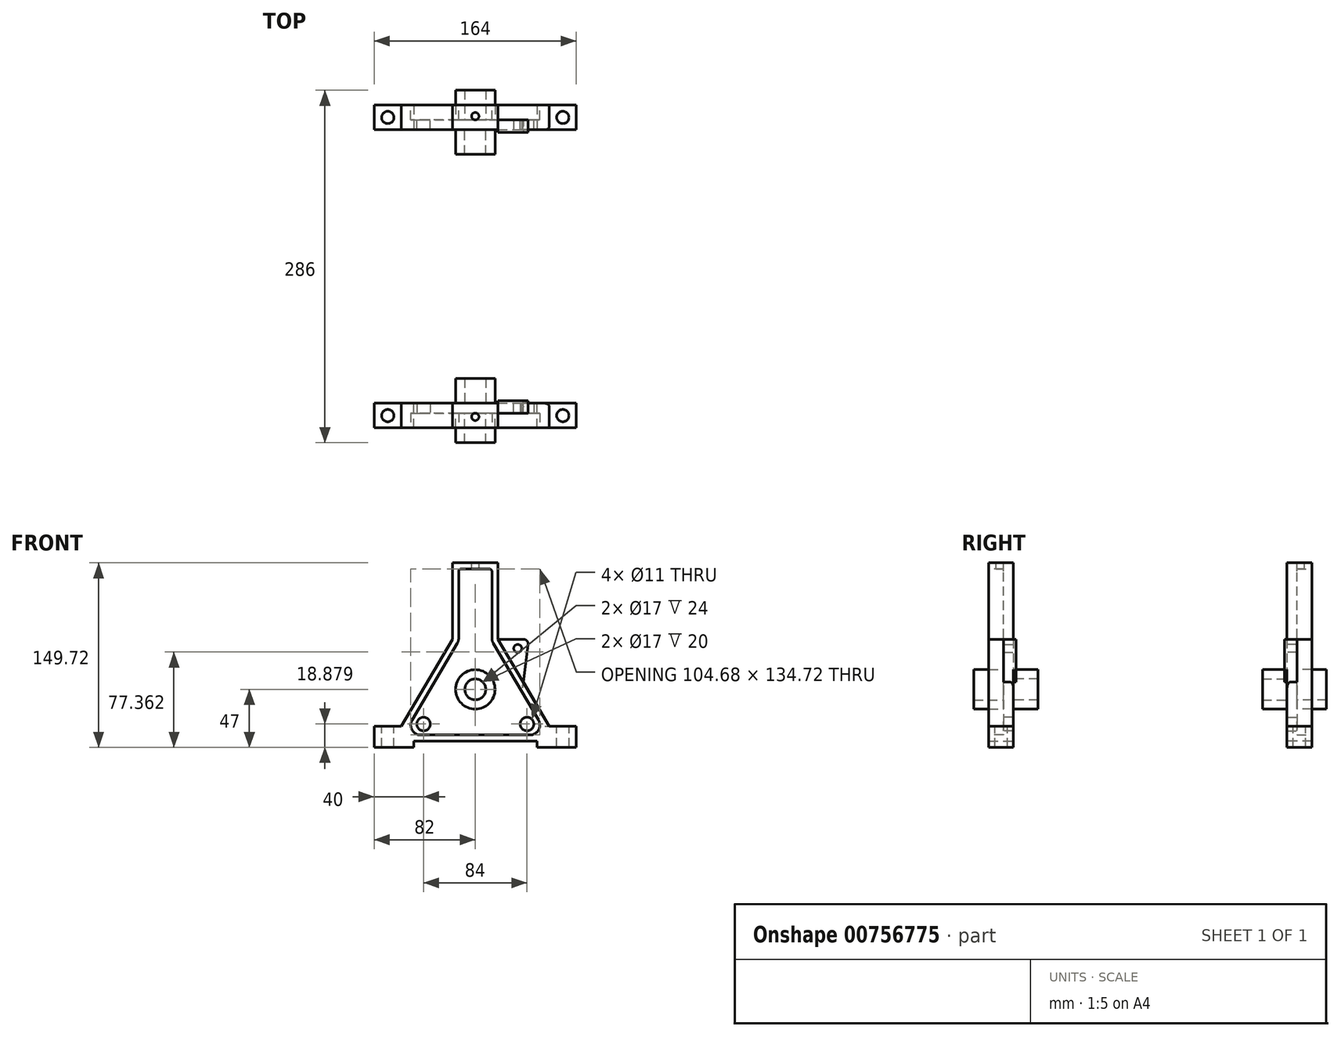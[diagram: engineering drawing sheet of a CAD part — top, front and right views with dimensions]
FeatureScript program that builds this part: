
annotation { "Feature Type Name" : "Feature", "Feature Type Description" : "" }
export const myFeature = defineFeature(function(context is Context, id is Id, definition is map)
    precondition{}
    {
        {
            var Q0;
            Q0=qCreatedBy(makeId("Front.planeOp"),FACE);
            var sketch = newSketch(context, id + "F0", { "sketchPlane" : qUnion([Q0])});
            skLineSegment(sketch, "E0", {"start": v(-18.5, 149.72) * mm, "end": v(-18.5, 87.72) * mm});
            skLineSegment(sketch, "E1", {"start": v(-18.5, 87.72) * mm, "end": v(-60, 17) * mm});
            skLineSegment(sketch, "E2", {"start": v(-60, 17) * mm, "end": v(-82, 17) * mm});
            skLineSegment(sketch, "E3", {"start": v(-82, 17) * mm, "end": v(-82, 0) * mm});
            skLineSegment(sketch, "E4", {"start": v(0, 0) * mm, "end": v(0, 149.72) * mm});
            skLineSegment(sketch, "E5", {"start": v(0, 149.72) * mm, "end": v(-18.5, 149.72) * mm});
            skLineSegment(sketch, "E6", {"start": v(-82, 0) * mm, "end": v(-50, 0) * mm});
            skLineSegment(sketch, "E7", {"start": v(-50, 0) * mm, "end": v(-50, 5) * mm});
            skLineSegment(sketch, "E8", {"start": v(-50, 5) * mm, "end": v(0, 5) * mm});
            skSolve(sketch);
        }
        {
            var Q0;
            Q0=makeQuery(id+"F0.imprint","IMPRINT",FACE,{"disambiguationData":[TD([[makeQuery(id+"F0.imprint","IMPRINT",EDGE,{"derivedFrom":sQuery(id+"F0.wireOp",EDGE,"E0")}),1.0]])]});
            extrude(context, id + "F1", {"entities" : qUnion([Q0]), "depth" : 20 * mm, "offsetDistance" : 25 * mm});
        }
        {
            var Q0;
            Q0=makeQuery(id+"F1.opExtrude","SWEPT_BODY",BODY,{"disambiguationData":[OSD([sQuery(id+"F0.wireOp",EDGE,"E0"),sQuery(id+"F0.wireOp",EDGE,"E1"),sQuery(id+"F0.wireOp",EDGE,"E2"),sQuery(id+"F0.wireOp",EDGE,"E3"),sQuery(id+"F0.wireOp",EDGE,"E4"),sQuery(id+"F0.wireOp",EDGE,"E5"),sQuery(id+"F0.wireOp",EDGE,"E6"),sQuery(id+"F0.wireOp",EDGE,"E7"),sQuery(id+"F0.wireOp",EDGE,"E8")])]});
            var Q1;
            Q1=qCreatedBy(makeId("Right.planeOp"),FACE);
            mirror(context, id + "F2", {"operationType" : NewBodyOperationType.ADD, "entities" : qUnion([Q0]), "mirrorPlane" : qUnion([Q1])});
        }
        {
            var Q0;
            {var subQ0=makeQuery(id+"F1.opExtrude","CAP_FACE",FACE,{"disambiguationData":[OSD([sQuery(id+"F0.wireOp",EDGE,"E0"),sQuery(id+"F0.wireOp",EDGE,"E1"),sQuery(id+"F0.wireOp",EDGE,"E2"),sQuery(id+"F0.wireOp",EDGE,"E3"),sQuery(id+"F0.wireOp",EDGE,"E4"),sQuery(id+"F0.wireOp",EDGE,"E5"),sQuery(id+"F0.wireOp",EDGE,"E6"),sQuery(id+"F0.wireOp",EDGE,"E7"),sQuery(id+"F0.wireOp",EDGE,"E8")])],"isStart":false});Q0=makeQuery(id+"F2.boolean.opBoolean","MERGE",FACE,{"derivedFrom":[subQ0,makeQuery(id+"F2.opPattern","COPY",FACE,{"derivedFrom":subQ0,"instanceName":"1"})]});}
            var sketch = newSketch(context, id + "F3", { "sketchPlane" : qUnion([Q0])});
            skLineSegment(sketch, "E9.7", {"start": v(51.24, 22.05) * mm, "end": v(14.6, 84.49) * mm});
            skLineSegment(sketch, "E9.8", {"start": v(13.5, 88.54) * mm, "end": v(13.5, 142.72) * mm});
            skLineSegment(sketch, "E9.9", {"start": v(11.5, 144.72) * mm, "end": v(-11.5, 144.72) * mm});
            skLineSegment(sketch, "E9.10", {"start": v(-44.34, 10) * mm, "end": v(44.34, 10) * mm});
            skLineSegment(sketch, "E9.11", {"start": v(-13.5, 142.72) * mm, "end": v(-13.5, 88.54) * mm});
            skLineSegment(sketch, "E9.12", {"start": v(-14.6, 84.49) * mm, "end": v(-51.24, 22.05) * mm});
            skArc(sketch, "E10.filletArc", {"start": v(-51.24, 22.05) * mm, "mid": v(-51.28, 14.02) * mm, "end": v(-44.34, 10) * mm});
            skArc(sketch, "E11.filletArc", {"start": v(44.34, 10) * mm, "mid": v(51.28, 14.02) * mm, "end": v(51.24, 22.05) * mm});
            skPoint(sketch, "E12.visualSharp", {"position": v(-13.5, 86.36) * mm});
            skArc(sketch, "E12.filletArc", {"start": v(-14.6, 84.49) * mm, "mid": v(-13.78, 86.44) * mm, "end": v(-13.5, 88.54) * mm});
            skPoint(sketch, "E13.visualSharp", {"position": v(13.5, 86.36) * mm});
            skArc(sketch, "E13.filletArc", {"start": v(13.5, 88.54) * mm, "mid": v(13.78, 86.44) * mm, "end": v(14.6, 84.49) * mm});
            skPoint(sketch, "E14.visualSharp", {"position": v(-13.5, 144.72) * mm});
            skArc(sketch, "E14.filletArc", {"start": v(-11.5, 144.72) * mm, "mid": v(-12.91, 144.14) * mm, "end": v(-13.5, 142.72) * mm});
            skPoint(sketch, "E15.visualSharp", {"position": v(13.5, 144.72) * mm});
            skArc(sketch, "E15.filletArc", {"start": v(13.5, 142.72) * mm, "mid": v(12.91, 144.14) * mm, "end": v(11.5, 144.72) * mm});
            skSolve(sketch);
        }
        {
            var Q0;
            Q0=makeQuery(id+"F3.imprint","IMPRINT",FACE,{"disambiguationData":[TD([[makeQuery(id+"F3.imprint","IMPRINT",EDGE,{"derivedFrom":sQuery(id+"F3.wireOp",EDGE,"E9.7")}),1.0]])]});
            extrude(context, id + "F4", {"entities" : qUnion([Q0]), "operationType" : NewBodyOperationType.REMOVE, "oppositeDirection" : true, "depth" : 12 * mm, "offsetDistance" : 25 * mm});
        }
        {
            var Q0;
            Q0=makeQuery(id+"F4.boolean.opBoolean","COPY",FACE,{"derivedFrom":makeQuery(id+"F4.opExtrude","CAP_FACE",FACE,{"disambiguationData":[OSD([sQuery(id+"F3.wireOp",EDGE,"E9.7"),sQuery(id+"F3.wireOp",EDGE,"E9.8"),sQuery(id+"F3.wireOp",EDGE,"E9.9"),sQuery(id+"F3.wireOp",EDGE,"E9.10"),sQuery(id+"F3.wireOp",EDGE,"E9.11"),sQuery(id+"F3.wireOp",EDGE,"E9.12"),sQuery(id+"F3.wireOp",EDGE,"E10.filletArc"),sQuery(id+"F3.wireOp",EDGE,"E11.filletArc"),sQuery(id+"F3.wireOp",EDGE,"E12.filletArc"),sQuery(id+"F3.wireOp",EDGE,"E13.filletArc"),sQuery(id+"F3.wireOp",EDGE,"E14.filletArc"),sQuery(id+"F3.wireOp",EDGE,"E15.filletArc")])],"isStart":false})});
            var sketch = newSketch(context, id + "F5", { "sketchPlane" : qUnion([Q0])});
            skCircle(sketch, "E16", {"center": v(-42, 18.88) * mm, "radius": 5.5 * mm});
            skCircle(sketch, "E17", {"center": v(42, 18.88) * mm, "radius": 5.5 * mm});
            skSolve(sketch);
        }
        {
            var Q0;
            Q0=makeQuery(id+"F5.imprint","IMPRINT",FACE,{"disambiguationData":[TD([[makeQuery(id+"F5.imprint","IMPRINT",EDGE,{"derivedFrom":sQuery(id+"F5.wireOp",EDGE,"E16")}),1.0]])]});
            var Q1;
            Q1=makeQuery(id+"F5.imprint","IMPRINT",FACE,{"disambiguationData":[TD([[makeQuery(id+"F5.imprint","IMPRINT",EDGE,{"derivedFrom":sQuery(id+"F5.wireOp",EDGE,"E17")}),1.0]])]});
            extrude(context, id + "F6", {"entities" : qUnion([Q0, Q1]), "operationType" : NewBodyOperationType.REMOVE, "oppositeDirection" : true, "depth" : 25 * mm, "offsetDistance" : 25 * mm});
        }
        {
            var Q0;
            Q0=makeQuery(id+"F4.boolean.opBoolean","COPY",FACE,{"derivedFrom":makeQuery(id+"F4.opExtrude","CAP_FACE",FACE,{"disambiguationData":[OSD([sQuery(id+"F3.wireOp",EDGE,"E9.7"),sQuery(id+"F3.wireOp",EDGE,"E9.8"),sQuery(id+"F3.wireOp",EDGE,"E9.9"),sQuery(id+"F3.wireOp",EDGE,"E9.10"),sQuery(id+"F3.wireOp",EDGE,"E9.11"),sQuery(id+"F3.wireOp",EDGE,"E9.12"),sQuery(id+"F3.wireOp",EDGE,"E10.filletArc"),sQuery(id+"F3.wireOp",EDGE,"E11.filletArc"),sQuery(id+"F3.wireOp",EDGE,"E12.filletArc"),sQuery(id+"F3.wireOp",EDGE,"E13.filletArc"),sQuery(id+"F3.wireOp",EDGE,"E14.filletArc"),sQuery(id+"F3.wireOp",EDGE,"E15.filletArc")])],"isStart":false})});
            var sketch = newSketch(context, id + "F7", { "sketchPlane" : qUnion([Q0])});
            skCircle(sketch, "E18", {"center": v(0, 47) * mm, "radius": 16 * mm});
            skCircle(sketch, "E19", {"center": v(0, 47) * mm, "radius": 8.5 * mm});
            skSolve(sketch);
        }
        {
            var Q0;
            Q0=makeQuery(id+"F7.imprint","IMPRINT",FACE,{"disambiguationData":[TD([[makeQuery(id+"F7.imprint","IMPRINT",EDGE,{"derivedFrom":sQuery(id+"F7.wireOp",EDGE,"E18")}),1.0]])]});
            extrude(context, id + "F8", {"entities" : qUnion([Q0]), "operationType" : NewBodyOperationType.ADD, "depth" : 24 * mm, "offsetDistance" : 25 * mm});
        }
        {
            var Q0;
            {var subQ0=makeQuery(id+"F1.opExtrude","CAP_FACE",FACE,{"disambiguationData":[OSD([sQuery(id+"F0.wireOp",EDGE,"E0"),sQuery(id+"F0.wireOp",EDGE,"E1"),sQuery(id+"F0.wireOp",EDGE,"E2"),sQuery(id+"F0.wireOp",EDGE,"E3"),sQuery(id+"F0.wireOp",EDGE,"E4"),sQuery(id+"F0.wireOp",EDGE,"E5"),sQuery(id+"F0.wireOp",EDGE,"E6"),sQuery(id+"F0.wireOp",EDGE,"E7"),sQuery(id+"F0.wireOp",EDGE,"E8")])],"isStart":true});Q0=makeQuery(id+"F2.boolean.opBoolean","MERGE",FACE,{"derivedFrom":[subQ0,makeQuery(id+"F2.opPattern","COPY",FACE,{"derivedFrom":subQ0,"instanceName":"1"})]});}
            var sketch = newSketch(context, id + "F9", { "sketchPlane" : qUnion([Q0])});
            skCircle(sketch, "E20.0.0", {"center": v(0, 47) * mm, "radius": 16 * mm});
            skCircle(sketch, "E21.0", {"center": v(0, 47) * mm, "radius": 8.5 * mm});
            skSolve(sketch);
        }
        {
            var Q0;
            Q0=makeQuery(id+"F9.imprint","IMPRINT",FACE,{"disambiguationData":[TD([[makeQuery(id+"F9.imprint","IMPRINT",EDGE,{"derivedFrom":sQuery(id+"F9.wireOp",EDGE,"E20.0.0")}),1.0]])]});
            extrude(context, id + "F10", {"entities" : qUnion([Q0]), "operationType" : NewBodyOperationType.ADD, "depth" : 20 * mm, "offsetDistance" : 25 * mm});
        }
        {
            var Q0;
            Q0=makeQuery(id+"F2.opPattern","COPY",FACE,{"derivedFrom":makeQuery(id+"F1.opExtrude","SWEPT_FACE",FACE,{"disambiguationData":[OSD([sQuery(id+"F0.wireOp",EDGE,"E2")])]}),"instanceName":"1"});
            var sketch = newSketch(context, id + "F11", { "sketchPlane" : qUnion([Q0])});
            skCircle(sketch, "E22", {"center": v(71, -10) * mm, "radius": 5 * mm});
            skPoint(sketch, "E22.centerSnap0", {"position": v(82, -10) * mm});
            skPoint(sketch, "E22.centerSnap1", {"position": v(71, 0) * mm});
            skCircle(sketch, "E23", {"center": v(-71, -10) * mm, "radius": 5 * mm});
            skPoint(sketch, "E23.centerSnap0", {"position": v(60, -10) * mm});
            skSolve(sketch);
        }
        {
            var Q0;
            Q0=makeQuery(id+"F11.imprint","IMPRINT",FACE,{"disambiguationData":[TD([[makeQuery(id+"F11.imprint","IMPRINT",EDGE,{"derivedFrom":sQuery(id+"F11.wireOp",EDGE,"E23")}),1.0]])]});
            var Q1;
            Q1=makeQuery(id+"F11.imprint","IMPRINT",FACE,{"disambiguationData":[TD([[makeQuery(id+"F11.imprint","IMPRINT",EDGE,{"derivedFrom":sQuery(id+"F11.wireOp",EDGE,"E22")}),1.0]])]});
            extrude(context, id + "F12", {"entities" : qUnion([Q0, Q1]), "operationType" : NewBodyOperationType.REMOVE, "oppositeDirection" : true, "depth" : 25 * mm, "offsetDistance" : 25 * mm});
        }
        {
            var Q0;
            {var subQ0=makeQuery(id+"F1.opExtrude","SWEPT_FACE",FACE,{"disambiguationData":[OSD([sQuery(id+"F0.wireOp",EDGE,"E5")])]});Q0=makeQuery(id+"F2.boolean.opBoolean","MERGE",FACE,{"derivedFrom":[subQ0,makeQuery(id+"F2.opPattern","COPY",FACE,{"derivedFrom":subQ0,"instanceName":"1"})]});}
            var sketch = newSketch(context, id + "F13", { "sketchPlane" : qUnion([Q0])});
            skCircle(sketch, "E24", {"center": v(0, -11) * mm, "radius": 3 * mm});
            skSolve(sketch);
        }
        {
            var Q0;
            Q0=makeQuery(id+"F13.imprint","IMPRINT",FACE,{"disambiguationData":[TD([[makeQuery(id+"F13.imprint","IMPRINT",EDGE,{"derivedFrom":sQuery(id+"F13.wireOp",EDGE,"E24")}),1.0]])]});
            extrude(context, id + "F14", {"entities" : qUnion([Q0]), "operationType" : NewBodyOperationType.REMOVE, "oppositeDirection" : true, "depth" : 10 * mm, "offsetDistance" : 25 * mm});
        }
        {
            var Q0;
            {var subQ0=sQuery(id+"F0.wireOp",EDGE,"E8");var subQ2=sQuery(id+"F0.wireOp",EDGE,"E7");var subQ4=sQuery(id+"F0.wireOp",EDGE,"E0");var subQ5=makeQuery(id+"F1.opExtrude","SWEPT_FACE",FACE,{"disambiguationData":[OSD([subQ4])]});var subQ6=sQuery(id+"F0.wireOp",EDGE,"E6");var subQ8=sQuery(id+"F0.wireOp",EDGE,"E1");var subQ10=sQuery(id+"F0.wireOp",EDGE,"E5");var subQ12=sQuery(id+"F0.wireOp",EDGE,"E3");var subQ14=sQuery(id+"F0.wireOp",EDGE,"E2");var subQ16=makeQuery(id+"F1.opExtrude","CAP_FACE",FACE,{"disambiguationData":[OSD([subQ4,subQ8,subQ14,subQ12,sQuery(id+"F0.wireOp",EDGE,"E4"),subQ10,subQ6,subQ2,subQ0])],"isStart":true});Q0=makeQuery(id+"F10.boolean.opBoolean","SPLIT",FACE,{"disambiguationData":[TD([subQ5])],"derivedFrom":makeQuery(id+"F2.boolean.opBoolean","MERGE",FACE,{"derivedFrom":[subQ16,makeQuery(id+"F2.opPattern","COPY",FACE,{"derivedFrom":subQ16,"instanceName":"1"})]})});}
            cPlane(context, id + "F15", {"entities" : qUnion([Q0]), "cplaneType" : CPlaneType.OFFSET, "offset" : 111 * mm, "width" : 150 * mm, "height" : 150 * mm});
        }
        {
            var Q0;
            {var subQ0=sQuery(id+"F0.wireOp",EDGE,"E8");var subQ2=sQuery(id+"F0.wireOp",EDGE,"E7");var subQ4=sQuery(id+"F0.wireOp",EDGE,"E0");var subQ5=makeQuery(id+"F1.opExtrude","SWEPT_FACE",FACE,{"disambiguationData":[OSD([subQ4])]});var subQ6=sQuery(id+"F0.wireOp",EDGE,"E6");var subQ8=sQuery(id+"F0.wireOp",EDGE,"E1");var subQ10=sQuery(id+"F0.wireOp",EDGE,"E5");var subQ12=sQuery(id+"F0.wireOp",EDGE,"E3");var subQ14=sQuery(id+"F0.wireOp",EDGE,"E2");var subQ16=makeQuery(id+"F1.opExtrude","CAP_FACE",FACE,{"disambiguationData":[OSD([subQ4,subQ8,subQ14,subQ12,sQuery(id+"F0.wireOp",EDGE,"E4"),subQ10,subQ6,subQ2,subQ0])],"isStart":true});Q0=makeQuery(id+"F10.boolean.opBoolean","SPLIT",FACE,{"disambiguationData":[TD([subQ5])],"derivedFrom":makeQuery(id+"F2.boolean.opBoolean","MERGE",FACE,{"derivedFrom":[subQ16,makeQuery(id+"F2.opPattern","COPY",FACE,{"derivedFrom":subQ16,"instanceName":"1"})]})});}
            var sketch = newSketch(context, id + "F16", { "sketchPlane" : qUnion([Q0])});
            skLineSegment(sketch, "E25", {"start": v(-18.5, 87.72) * mm, "end": v(-38.93, 87.72) * mm});
            skLineSegment(sketch, "E26", {"start": v(-42.9, 83.2) * mm, "end": v(-38.86, 53.03) * mm});
            skCircle(sketch, "E27", {"center": v(-34.42, 80.22) * mm, "radius": 3.25 * mm});
            skPoint(sketch, "E28.visualSharp", {"position": v(-43.5, 87.72) * mm});
            skArc(sketch, "E28.filletArc", {"start": v(-38.93, 87.72) * mm, "mid": v(-41.94, 86.36) * mm, "end": v(-42.9, 83.2) * mm});
            skSolve(sketch);
        }
        {
            var Q0;
            {var subQ1=sQuery(id+"F16.wireOp",EDGE,"E25");Q0=makeQuery(id+"F16.imprint","IMPRINT",FACE,{"disambiguationData":[TD([[makeQuery(id+"F16.imprint","IMPRINT",EDGE,{"derivedFrom":subQ1}),1.0]])]});}
            extrude(context, id + "F17", {"entities" : qUnion([Q0]), "operationType" : NewBodyOperationType.ADD, "oppositeDirection" : true, "depth" : 8 * mm, "offsetDistance" : 25 * mm, "hasSecondDirection" : true, "secondDirectionOppositeDirection" : false, "secondDirectionDepth" : 2 * mm});
        }
        {
            var Q0;
            {var subQ0=sQuery(id+"F0.wireOp",EDGE,"E1");Q0=makeQuery(id+"F17.boolean.opBoolean","SPLIT",EDGE,{"disambiguationData":[topologyDisambiguationEdgeConnected([makeQuery(id+"F17.opExtrude","SWEPT_FACE",FACE,{"disambiguationData":[OSD([subQ0])]})])],"derivedFrom":makeQuery(id+"F2.opPattern","COPY",EDGE,{"derivedFrom":makeQuery(id+"F1.opExtrude","CAP_EDGE",EDGE,{"disambiguationData":[OSD([subQ0])],"isStart":true}),"instanceName":"1"})});}
            fillet(context, id + "F18", {"entities" : qUnion([Q0]), "radius" : 3 * mm, "tangentPropagation" : true, "allowEdgeOverflow" : false});
        }
        {
            var Q0;
            Q0=makeQuery(id+"F1.opExtrude","SWEPT_BODY",BODY,{"disambiguationData":[OSD([sQuery(id+"F0.wireOp",EDGE,"E0"),sQuery(id+"F0.wireOp",EDGE,"E1"),sQuery(id+"F0.wireOp",EDGE,"E2"),sQuery(id+"F0.wireOp",EDGE,"E3"),sQuery(id+"F0.wireOp",EDGE,"E4"),sQuery(id+"F0.wireOp",EDGE,"E5"),sQuery(id+"F0.wireOp",EDGE,"E6"),sQuery(id+"F0.wireOp",EDGE,"E7"),sQuery(id+"F0.wireOp",EDGE,"E8")])]});
            var Q1;
            Q1=qCreatedBy(id+"F15.planeOp",FACE);
            mirror(context, id + "F19", {"entities" : qUnion([Q0]), "mirrorPlane" : qUnion([Q1])});
        }
    });
